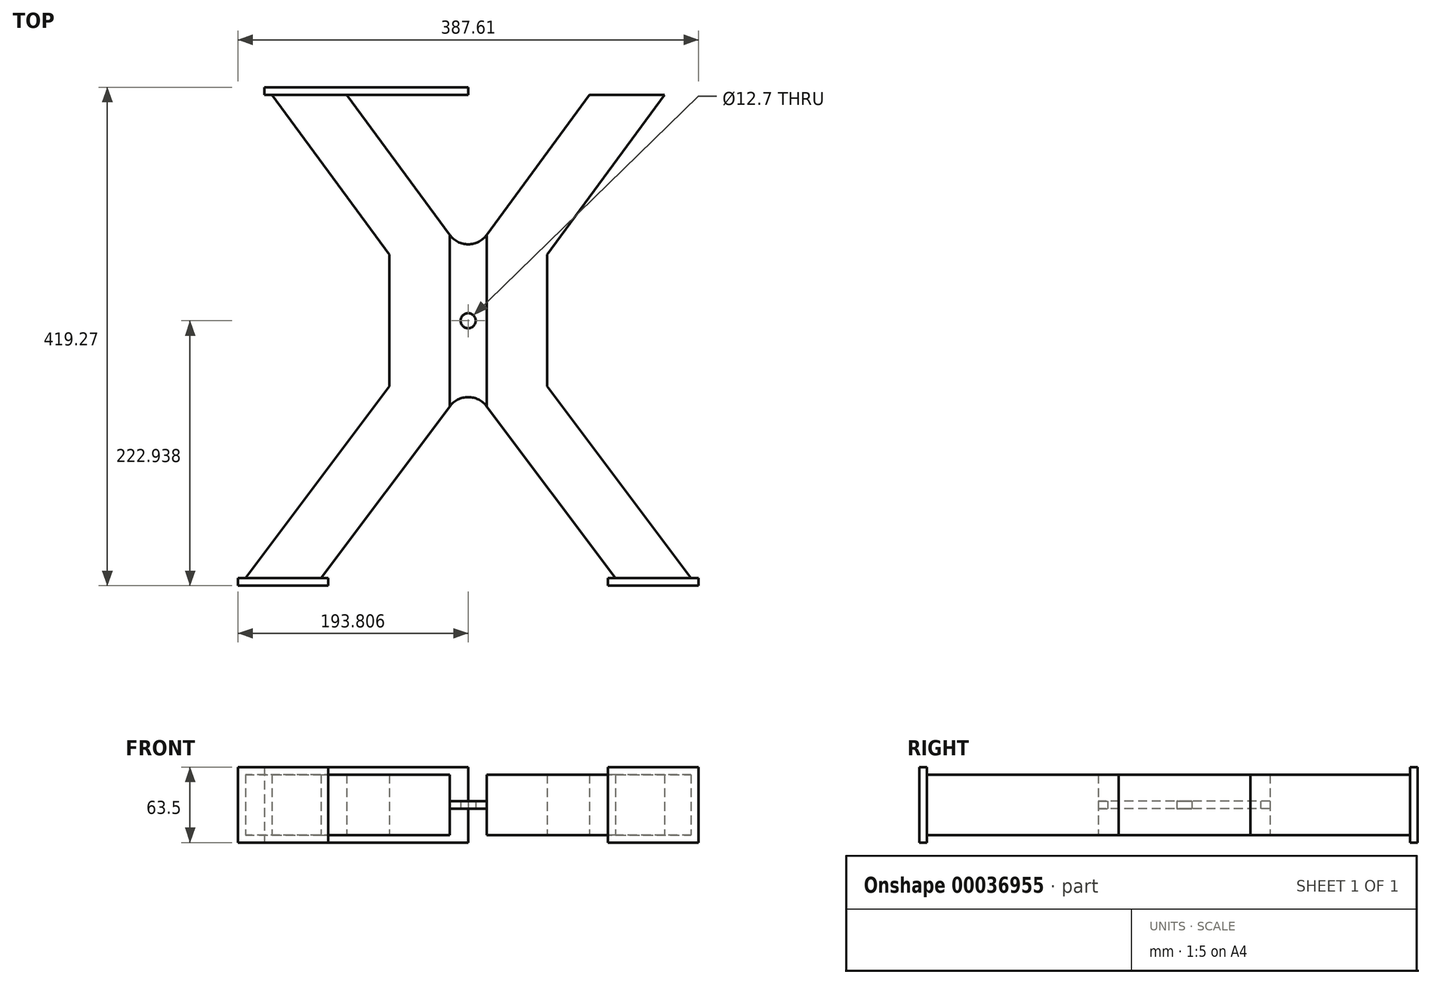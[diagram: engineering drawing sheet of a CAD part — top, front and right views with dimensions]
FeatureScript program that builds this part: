
annotation { "Feature Type Name" : "Feature", "Feature Type Description" : "" }
export const myFeature = defineFeature(function(context is Context, id is Id, definition is map)
    precondition{}
    {
        {
            var Q0;
            Q0=qCreatedBy(makeId("Top.planeOp"),FACE);
            var sketch = newSketch(context, id + "F0", { "sketchPlane" : qUnion([Q0])});
            skLineSegment(sketch, "E0", {"start": v(73.16, 457.37) * mm, "end": v(171.77, 322.98) * mm});
            skLineSegment(sketch, "E1", {"start": v(222.57, 339.62) * mm, "end": v(136.16, 457.37) * mm});
            skLineSegment(sketch, "E2", {"start": v(136.16, 457.37) * mm, "end": v(73.16, 457.37) * mm});
            skLineSegment(sketch, "E3", {"start": v(171.77, 322.98) * mm, "end": v(171.77, 267.54) * mm});
            skLineSegment(sketch, "E4", {"start": v(222.57, 267.54) * mm, "end": v(171.77, 267.54) * mm, "construction": true});
            skLineSegment(sketch, "E5.MirrorCS", {"start": v(171.77, 212.09) * mm, "end": v(171.77, 267.54) * mm});
            skLineSegment(sketch, "E6", {"start": v(222.57, 339.62) * mm, "end": v(222.57, 195.16) * mm});
            skLineSegment(sketch, "E7", {"start": v(171.77, 212.09) * mm, "end": v(50.8, 50.8) * mm});
            skLineSegment(sketch, "E8", {"start": v(50.8, 50.8) * mm, "end": v(114.3, 50.8) * mm});
            skLineSegment(sketch, "E9", {"start": v(114.3, 50.8) * mm, "end": v(222.57, 195.16) * mm});
            skLineSegment(sketch, "E10", {"start": v(238.26, 457.37) * mm, "end": v(238.26, 50.8) * mm, "construction": true});
            skLineSegment(sketch, "E11.bottom", {"start": v(66.8, 463.72) * mm, "end": v(238.26, 463.72) * mm});
            skLineSegment(sketch, "E11.top", {"start": v(66.8, 457.37) * mm, "end": v(238.26, 457.37) * mm});
            skLineSegment(sketch, "E11.left", {"start": v(66.8, 463.72) * mm, "end": v(66.8, 457.37) * mm});
            skLineSegment(sketch, "E11.right", {"start": v(238.26, 463.72) * mm, "end": v(238.26, 457.37) * mm});
            skLineSegment(sketch, "E12.MirrorCS", {"start": v(409.7, 463.72) * mm, "end": v(409.7, 457.37) * mm});
            skLineSegment(sketch, "E13.MirrorCS", {"start": v(340.35, 457.37) * mm, "end": v(403.36, 457.37) * mm});
            skLineSegment(sketch, "E14.MirrorCS", {"start": v(403.36, 457.37) * mm, "end": v(304.74, 322.98) * mm});
            skLineSegment(sketch, "E15.MirrorCS", {"start": v(425.71, 50.8) * mm, "end": v(362.21, 50.8) * mm});
            skLineSegment(sketch, "E16.MirrorCS", {"start": v(362.21, 50.8) * mm, "end": v(253.94, 195.16) * mm});
            skLineSegment(sketch, "E17.MirrorCS", {"start": v(304.74, 212.09) * mm, "end": v(304.74, 267.54) * mm});
            skLineSegment(sketch, "E18.MirrorCS", {"start": v(304.74, 212.09) * mm, "end": v(425.71, 50.8) * mm});
            skLineSegment(sketch, "E19.MirrorCS", {"start": v(253.94, 339.62) * mm, "end": v(253.94, 195.16) * mm});
            skLineSegment(sketch, "E20.MirrorCS", {"start": v(253.94, 339.62) * mm, "end": v(340.35, 457.37) * mm});
            skLineSegment(sketch, "E21.MirrorCS", {"start": v(253.94, 267.54) * mm, "end": v(304.74, 267.54) * mm});
            skLineSegment(sketch, "E22.MirrorCS", {"start": v(409.7, 463.72) * mm, "end": v(238.26, 463.72) * mm});
            skLineSegment(sketch, "E23.MirrorCS", {"start": v(304.74, 322.98) * mm, "end": v(304.74, 267.54) * mm});
            skLineSegment(sketch, "E24.MirrorCS", {"start": v(409.7, 457.37) * mm, "end": v(238.26, 457.37) * mm});
            skSolve(sketch);
        }
        {
            var Q0;
            {var subQ0=sQuery(id+"F0.wireOp",EDGE,"E0");Q0=makeQuery(id+"F0.imprint","IMPRINT",FACE,{"disambiguationData":[TD([[makeQuery(id+"F0.imprint","IMPRINT",EDGE,{"derivedFrom":subQ0}),1.0]])]});}
            var Q1;
            Q1=makeQuery(id+"F0.imprint","IMPRINT",FACE,{"disambiguationData":[TD([[makeQuery(id+"F0.imprint","IMPRINT",EDGE,{"derivedFrom":sQuery(id+"F0.wireOp",EDGE,"E15.MirrorCS")}),-1.0]])]});
            var Q2;
            {var subQ0=sQuery(id+"F0.wireOp",EDGE,"E14.MirrorCS");Q2=makeQuery(id+"F0.imprint","IMPRINT",FACE,{"disambiguationData":[TD([[makeQuery(id+"F0.imprint","IMPRINT",EDGE,{"derivedFrom":subQ0}),-1.0]])]});}
            extrude(context, id + "F1", {"entities" : qUnion([Q0, Q1, Q2]), "depth" : 50.8 * mm});
        }
        {
            var Q0;
            Q0=makeQuery(id+"F1.opExtrude","CAP_FACE",FACE,{"disambiguationData":[OSD([sQuery(id+"F0.wireOp",EDGE,"E0"),sQuery(id+"F0.wireOp",EDGE,"E1"),sQuery(id+"F0.wireOp",EDGE,"E2"),sQuery(id+"F0.wireOp",EDGE,"E3"),sQuery(id+"F0.wireOp",EDGE,"E5.MirrorCS"),sQuery(id+"F0.wireOp",EDGE,"E6"),sQuery(id+"F0.wireOp",EDGE,"E7"),sQuery(id+"F0.wireOp",EDGE,"E8"),sQuery(id+"F0.wireOp",EDGE,"E9")])],"isStart":false});
            var sketch = newSketch(context, id + "F2", { "sketchPlane" : qUnion([Q0])});
            skSolve(sketch);
        }
        {
            var Q0;
            Q0=makeQuery(id+"F0.imprint","IMPRINT",FACE,{"disambiguationData":[TD([[makeQuery(id+"F0.imprint","IMPRINT",EDGE,{"derivedFrom":sQuery(id+"F0.wireOp",EDGE,"E11.bottom")}),-1.0]])]});
            var Q1;
            {var subQ2=sQuery(id+"F0.wireOp",EDGE,"E11.right");Q1=makeQuery(id+"F0.imprint","IMPRINT",FACE,{"disambiguationData":[TD([[makeQuery(id+"F0.imprint","IMPRINT",EDGE,{"derivedFrom":subQ2}),1.0]])]});}
            extrude(context, id + "F3", {"entities" : qUnion([Q0, Q1]), "operationType" : NewBodyOperationType.ADD, "depth" : 57.15 * mm, "hasSecondDirection" : true, "secondDirectionOppositeDirection" : true, "secondDirectionDepth" : 6.35 * mm});
        }
        {
            var Q0;
            Q0=makeQuery(id+"F2.imprint","IMPRINT",FACE,{"disambiguationData":[TD([[makeQuery(id+"F2.imprint","IMPRINT",EDGE,{"derivedFrom":makeQuery(id+"F1.opExtrude","CAP_EDGE",EDGE,{"disambiguationData":[OSD([sQuery(id+"F0.wireOp",EDGE,"E0")])],"isStart":false})}),1.0]])]});
            var sketch = newSketch(context, id + "F4", { "sketchPlane" : qUnion([Q0])});
            skLineSegment(sketch, "E25.bottom", {"start": v(44.45, 50.8) * mm, "end": v(120.65, 50.8) * mm});
            skLineSegment(sketch, "E25.top", {"start": v(44.45, 44.45) * mm, "end": v(120.65, 44.45) * mm});
            skLineSegment(sketch, "E25.left", {"start": v(44.45, 50.8) * mm, "end": v(44.45, 44.45) * mm});
            skLineSegment(sketch, "E25.right", {"start": v(120.65, 50.8) * mm, "end": v(120.65, 44.45) * mm});
            skLineSegment(sketch, "E26", {"start": v(50.8, 50.8) * mm, "end": v(50.8, 44.45) * mm, "construction": true});
            skLineSegment(sketch, "E27", {"start": v(114.3, 50.8) * mm, "end": v(114.3, 44.45) * mm, "construction": true});
            skLineSegment(sketch, "E28.MirrorCS", {"start": v(432.06, 50.8) * mm, "end": v(432.06, 44.45) * mm});
            skLineSegment(sketch, "E29.MirrorCS", {"start": v(355.86, 50.8) * mm, "end": v(355.86, 44.45) * mm});
            skLineSegment(sketch, "E30.MirrorCS", {"start": v(425.71, 50.8) * mm, "end": v(425.71, 44.45) * mm});
            skLineSegment(sketch, "E31.MirrorCS", {"start": v(362.21, 50.8) * mm, "end": v(362.21, 44.45) * mm});
            skLineSegment(sketch, "E32.MirrorCS", {"start": v(432.06, 50.8) * mm, "end": v(355.86, 50.8) * mm});
            skLineSegment(sketch, "E33.MirrorCS", {"start": v(432.06, 44.45) * mm, "end": v(355.86, 44.45) * mm});
            skSolve(sketch);
        }
        {
            var Q0;
            Q0 = qSketchRegion(id + "F4", true);
            extrude(context, id + "F5", {"entities" : qUnion([Q0]), "operationType" : NewBodyOperationType.ADD, "depth" : 6.35 * mm, "hasSecondDirection" : true, "secondDirectionOppositeDirection" : true, "secondDirectionDepth" : 57.15 * mm});
        }
        {
            var Q0;
            Q0=qCreatedBy(makeId("Top.planeOp"),FACE);
            cPlane(context, id + "F6", {"entities" : qUnion([Q0]), "cplaneType" : CPlaneType.OFFSET, "offset" : 25.4 * mm, "width" : 152.4 * mm, "height" : 152.4 * mm});
        }
        {
            var Q0;
            Q0=qCreatedBy(id+"F6.planeOp",FACE);
            var sketch = newSketch(context, id + "F7", { "sketchPlane" : qUnion([Q0])});
            skLineSegment(sketch, "E34.0", {"start": v(222.57, 339.62) * mm, "end": v(222.57, 195.16) * mm});
            skLineSegment(sketch, "E34.1", {"start": v(253.94, 339.62) * mm, "end": v(253.94, 195.16) * mm});
            skArc(sketch, "E35", {"start": v(222.57, 339.62) * mm, "mid": v(238.26, 331.67) * mm, "end": v(253.94, 339.62) * mm});
            skPoint(sketch, "E35.third.point", {"position": v(248.77, 367.5) * mm});
            skLineSegment(sketch, "E36", {"start": v(253.94, 267.39) * mm, "end": v(222.57, 267.39) * mm, "construction": true});
            skLineSegment(sketch, "E37.0", {"start": v(222.57, 339.62) * mm, "end": v(136.16, 457.37) * mm, "construction": true});
            skLineSegment(sketch, "E37.1", {"start": v(253.94, 339.62) * mm, "end": v(340.35, 457.37) * mm, "construction": true});
            skArc(sketch, "E38.MirrorCS", {"start": v(222.57, 195.16) * mm, "mid": v(238.26, 203.1) * mm, "end": v(253.94, 195.16) * mm});
            skCircle(sketch, "E39", {"center": v(238.26, 267.39) * mm, "radius": 6.35 * mm});
            skSolve(sketch);
        }
        {
            var Q0;
            Q0 = qSketchRegion(id + "F7", true);
            extrude(context, id + "F8", {"entities" : qUnion([Q0]), "depth" : 3.17 * mm, "hasSecondDirection" : true, "secondDirectionOppositeDirection" : true, "secondDirectionDepth" : 3.17 * mm});
        }
    });
